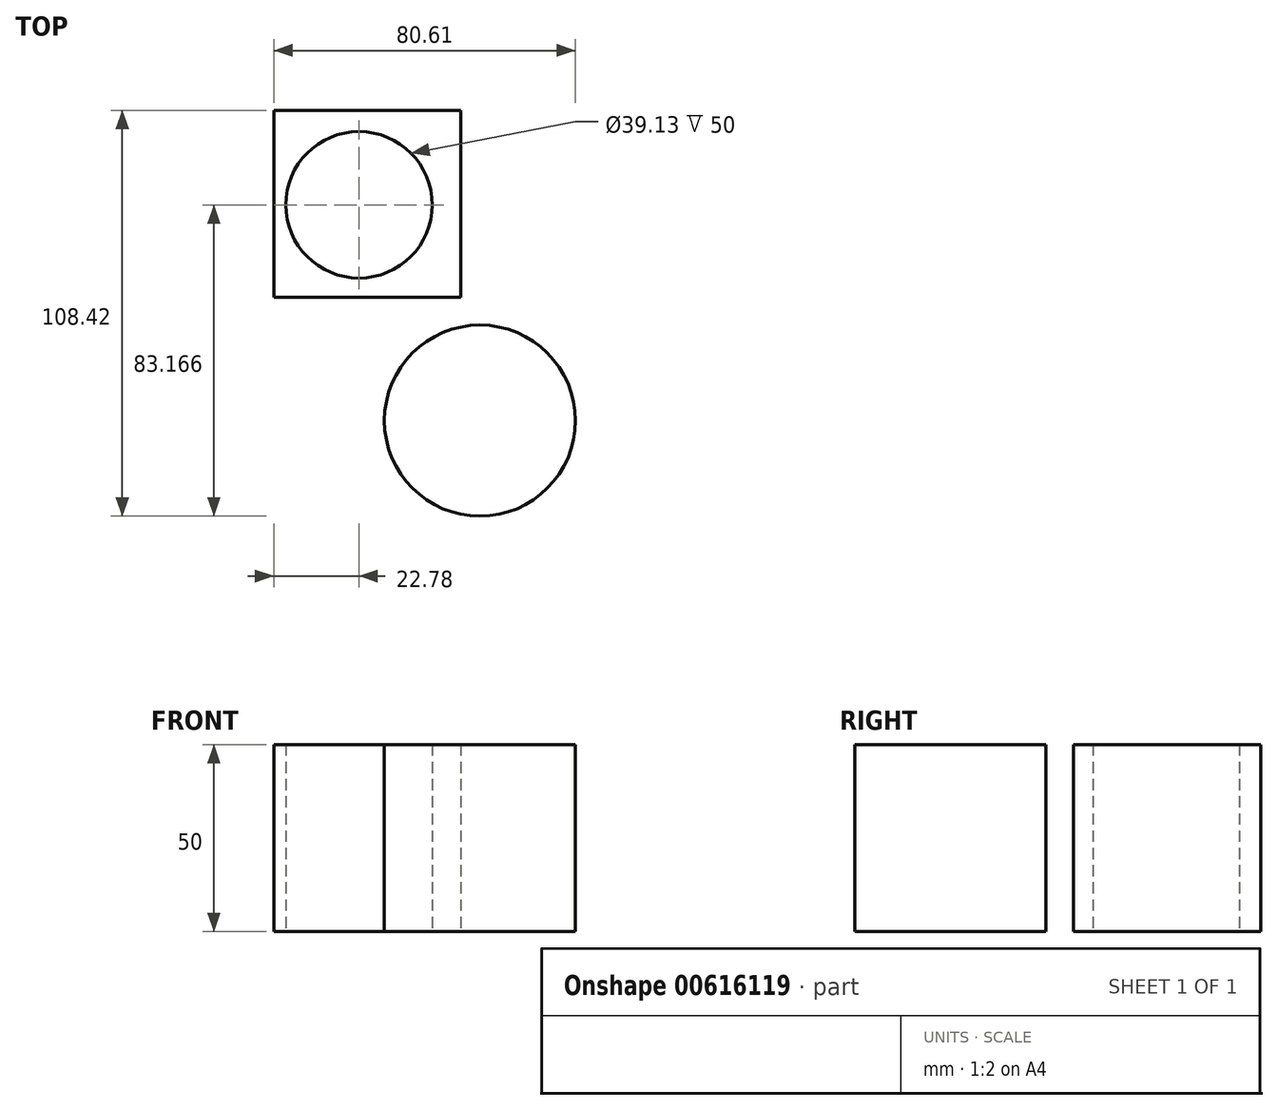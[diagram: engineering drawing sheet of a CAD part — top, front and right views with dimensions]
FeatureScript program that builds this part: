
annotation { "Feature Type Name" : "Feature", "Feature Type Description" : "" }
export const myFeature = defineFeature(function(context is Context, id is Id, definition is map)
    precondition{}
    {
        {
            var Q0;
            Q0=qCreatedBy(makeId("Top.planeOp"),FACE);
            var sketch = newSketch(context, id + "F0", { "sketchPlane" : qUnion([Q0])});
            skLineSegment(sketch, "E0.bottom", {"start": v(0, 0) * mm, "end": v(-50, 0) * mm});
            skLineSegment(sketch, "E0.top", {"start": v(0, 50) * mm, "end": v(-50, 50) * mm});
            skLineSegment(sketch, "E0.left", {"start": v(0, 0) * mm, "end": v(0, 50) * mm});
            skLineSegment(sketch, "E0.right", {"start": v(-50, 0) * mm, "end": v(-50, 50) * mm});
            skSolve(sketch);
        }
        {
            var Q0;
            Q0 = qSketchRegion(id + "F0", true);
            var Q1;
            Q1 = qConstructionFilter(qBodyType(qCreatedBy(id + "F0" ,EDGE), BodyType.WIRE), ConstructionObject.NO);
            extrude(context, id + "F1", {"entities" : qUnion([Q0]), "surfaceEntities" : qUnion([Q1]), "depth" : 50 * mm, "offsetDistance" : 25 * mm});
        }
        {
            var Q0;
            Q0=qCreatedBy(makeId("Top.planeOp"),FACE);
            var sketch = newSketch(context, id + "F2", { "sketchPlane" : qUnion([Q0])});
            skCircle(sketch, "E1", {"center": v(5.1, -32.9) * mm, "radius": 25.52 * mm});
            skSolve(sketch);
        }
        {
            var Q0;
            Q0 = qSketchRegion(id + "F2", true);
            extrude(context, id + "F3", {"entities" : qUnion([Q0]), "depth" : 50 * mm, "offsetDistance" : 25 * mm});
        }
        {
            var Q0;
            Q0=qCreatedBy(makeId("Top.planeOp"),FACE);
            var sketch = newSketch(context, id + "F4", { "sketchPlane" : qUnion([Q0])});
            skCircle(sketch, "E2", {"center": v(-28.1, 25.04) * mm, "radius": 14.91 * mm});
            skSolve(sketch);
        }
        {
            var Q0;
            Q0 = qSketchRegion(id + "F4", true);
            extrude(context, id + "F5", {"entities" : qUnion([Q0]), "operationType" : NewBodyOperationType.REMOVE, "oppositeDirection" : true, "depth" : 50 * mm, "offsetDistance" : 25 * mm});
        }
        {
            var Q0;
            Q0=qCreatedBy(makeId("Top.planeOp"),FACE);
            var sketch = newSketch(context, id + "F6", { "sketchPlane" : qUnion([Q0])});
            skCircle(sketch, "E3", {"center": v(-27.22, 24.75) * mm, "radius": 19.57 * mm});
            skSolve(sketch);
        }
        {
            var Q0;
            Q0 = qSketchRegion(id + "F6", true);
            extrude(context, id + "F7", {"entities" : qUnion([Q0]), "operationType" : NewBodyOperationType.REMOVE, "depth" : 50 * mm, "offsetDistance" : 25 * mm});
        }
    });
